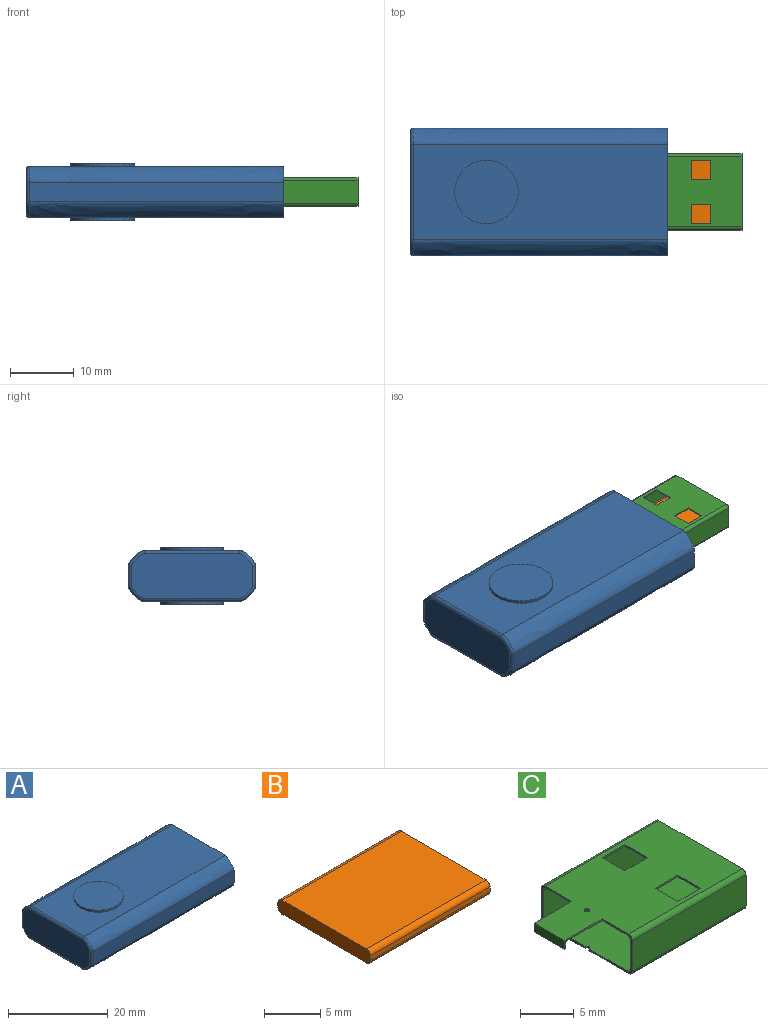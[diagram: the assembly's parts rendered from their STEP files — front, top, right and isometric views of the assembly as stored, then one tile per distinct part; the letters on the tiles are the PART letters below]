
ASSEMBLY  parts=3 mates=2
PART A: 31 faces, bbox 44.5x20.5x9.5 mm
  f0: plane 40x3mm, normal (0,1,0), area 120mm2, adj f12,f14,f16,f21
  f1: plane 40x15mm, normal (0,0,1), area 521.5mm2, adj f12,f15,f16,f25,f27
  f2: plane 40x3mm, normal (0,-1,0), area 120mm2, adj f12,f13,f15,f24
  f3: plane 40x11mm, normal (0,0,-1), area 440mm2, adj f4,f10,f12,f17
  f4: cylinder r=0.5mm len=40mm, axis (1,0,0), area 31.4mm2, adj f3,f5,f12,f17
  f5: plane 40x3.5mm, normal (0,-1,0), area 140mm2, adj f4,f6,f12,f17
  f6: cylinder r=0.5mm len=40mm, axis (1,0,0), area 31.4mm2, adj f5,f7,f12,f17
  f7: plane 40x11mm, normal (0,0,1), area 440mm2, adj f6,f8,f12,f17
  f8: cylinder r=0.5mm len=40mm, axis (1,0,0), area 31.4mm2, adj f7,f9,f12,f17
  f9: plane 40x3.5mm, normal (0,1,0), area 140mm2, adj f8,f10,f12,f17
  f10: cylinder r=0.5mm len=40mm, axis (1,0,0), area 31.4mm2, adj f3,f9,f12,f17
  f11: plane 40x15mm, normal (0,0,-1), area 521.5mm2, adj f12,f13,f14,f20,f29
  f12: plane 20.5x8.5mm, normal (1,0,0), area 98.3mm2, adj f0,f1,f2,f3,f4,f5,f6,f7
  f13: bspline ~44x2.5mm, area 149mm2, adj f2,f11,f12,f22
  f14: bspline ~44x2.5mm, area 149mm2, adj f0,f11,f12,f19
  f15: bspline ~44x2.5mm, area 149mm2, adj f1,f2,f12,f26
  f16: bspline ~44x2.5mm, area 149mm2, adj f0,f1,f12,f23
  f17: plane 12x4.5mm, normal (1,0,0), area 53.8mm2, adj f3,f4,f5,f6,f7,f8,f9,f10
  f18: plane 19x7mm, normal (-1,0,0), area 127.5mm2, adj f19,f20,f21,f22,f23,f24,f25,f26
  f19: bspline ~3.12x2.74mm, area 2.7mm2, adj f14,f18,f20,f21
  f20: cylinder r=0.5mm len=15mm, axis (0,1,0), area 11.8mm2, adj f11,f18,f19,f22
  f21: cylinder r=0.5mm len=3mm, axis (0,0,1), area 2.4mm2, adj f0,f18,f19,f23
  f22: bspline ~3.12x2.74mm, area 2.7mm2, adj f13,f18,f20,f24
  f23: bspline ~3.12x2.74mm, area 2.7mm2, adj f16,f18,f21,f25
  f24: cylinder r=0.5mm len=3mm, axis (0,0,-1), area 2.4mm2, adj f2,f18,f22,f26
  f25: cylinder r=0.5mm len=15mm, axis (0,-1,0), area 11.8mm2, adj f1,f18,f23,f26
  f26: bspline ~3.12x2.74mm, area 2.7mm2, adj f15,f18,f24,f25
  f27: cylinder r=5mm len=10mm, axis (0,0,-1), area 15.7mm2, adj f1,f28
  f28: plane 10x10mm, normal (0,0,1), area 78.5mm2, adj f27
  f29: cylinder r=5mm len=10mm, axis (0,0,1), area 15.7mm2, adj f11,f30
  f30: plane 10x10mm, normal (0,0,-1), area 78.5mm2, adj f29
PART B: 10 faces, bbox 15x11.6x1.5 mm
  f0: plane 11.6x1.5mm, normal (-1,0,0), area 17.2mm2, adj f1,f2,f3,f4,f5,f6,f7,f8
  f1: plane 15x0.5mm, normal (0,-1,0), area 7.5mm2, adj f0,f2,f8,f9
  f2: cylinder r=0.5mm len=15mm, axis (1,0,0), area 11.8mm2, adj f0,f1,f3,f9
  f3: plane 15x10.6mm, normal (0,0,-1), area 159mm2, adj f0,f2,f4,f9
  f4: cylinder r=0.5mm len=15mm, axis (1,0,0), area 11.8mm2, adj f0,f3,f5,f9
  f5: plane 15x0.5mm, normal (0,1,0), area 7.5mm2, adj f0,f4,f6,f9
  f6: cylinder r=0.5mm len=15mm, axis (1,0,0), area 11.8mm2, adj f0,f5,f7,f9
  f7: plane 15x10.6mm, normal (0,0,1), area 159mm2, adj f0,f6,f8,f9
  f8: cylinder r=0.5mm len=15mm, axis (1,0,0), area 11.8mm2, adj f0,f1,f7,f9
  f9: plane 11.6x1.5mm, normal (1,0,0), area 17.2mm2, adj f1,f2,f3,f4,f5,f6,f7,f8
PART C: 42 faces, bbox 20x12x4.5 mm
  f0: cylinder r=0.25mm len=0.5mm, axis (0,0,-1), area 0.2mm2, adj f10,f11,f24,f31
  f1: plane 12x4.5mm, normal (1,0,0), area 6.4mm2, adj f13,f14,f23,f24,f29,f30,f31,f32
  f2: plane 3x0.2mm, normal (0,1,0), area 0.6mm2, adj f3,f8,f24,f31
  f3: plane 3x0.2mm, normal (1,0,0), area 0.6mm2, adj f2,f4,f24,f31
  f4: plane 3x0.2mm, normal (0,-1,0), area 0.6mm2, adj f3,f8,f24,f31
  f5: plane 3x0.2mm, normal (1,0,0), area 0.6mm2, adj f6,f9,f24,f31
  f6: plane 3x0.2mm, normal (0,-1,0), area 0.6mm2, adj f5,f7,f24,f31
  f7: plane 3x0.2mm, normal (-1,0,0), area 0.6mm2, adj f6,f9,f24,f31
  f8: plane 3x0.2mm, normal (-1,0,0), area 0.6mm2, adj f2,f4,f24,f31
  f9: plane 3x0.2mm, normal (0,1,0), area 0.6mm2, adj f5,f7,f24,f31
  f10: plane 5.75x4.5mm, normal (-1,0,0), area 2.8mm2, adj f0,f13,f23,f24,f27,f30,f31,f32
  f11: plane 5.75x4.5mm, normal (-1,0,0), area 2.8mm2, adj f0,f14,f23,f24,f25,f29,f31,f32
  f12: cylinder r=0.25mm len=0.5mm, axis (0,0,-1), area 0.3mm2, adj f23,f32
  f13: plane 15x3.5mm, normal (0,-1,0), area 52.5mm2, adj f1,f10,f39,f41
  f14: plane 15x3.5mm, normal (0,1,0), area 52.5mm2, adj f1,f11,f38,f40
  f15: plane 3x0.2mm, normal (0,1,0), area 0.6mm2, adj f16,f21,f23,f32
  f16: plane 3x0.2mm, normal (1,0,0), area 0.6mm2, adj f15,f17,f23,f32
  f17: plane 3x0.2mm, normal (0,-1,0), area 0.6mm2, adj f16,f21,f23,f32
  f18: plane 3x0.2mm, normal (1,0,0), area 0.6mm2, adj f19,f22,f23,f32
  f19: plane 3x0.2mm, normal (0,-1,0), area 0.6mm2, adj f18,f20,f23,f32
  f20: plane 3x0.2mm, normal (-1,0,0), area 0.6mm2, adj f19,f22,f23,f32
  f21: plane 3x0.2mm, normal (-1,0,0), area 0.6mm2, adj f15,f17,f23,f32
  f22: plane 3x0.2mm, normal (0,1,0), area 0.6mm2, adj f18,f20,f23,f32
  f23: plane 20x11mm, normal (0,0,1), area 166.8mm2, adj f1,f10,f11,f12,f15,f16,f17,f18
  f24: plane 15x11mm, normal (0,0,-1), area 146.9mm2, adj f0,f1,f2,f3,f4,f5,f6,f7
  f25: plane 5x1mm, normal (0,1,0), area 1.2mm2, adj f11,f23,f26,f28,f32,f33
  f26: plane 4x1mm, normal (-1,0,0), area 4mm2, adj f23,f25,f27,f28
  f27: plane 5x1mm, normal (0,-1,0), area 1.2mm2, adj f10,f23,f26,f28,f32,f33
  f28: plane 4x0.2mm, normal (0,0,-1), area 0.8mm2, adj f25,f26,f27,f33
  f29: plane 15x3.1mm, normal (0,-1,0), area 46.5mm2, adj f1,f11,f34,f36
  f30: plane 15x3.1mm, normal (0,1,0), area 46.5mm2, adj f1,f10,f35,f37
  f31: plane 15x10.6mm, normal (0,0,1), area 140.9mm2, adj f0,f1,f2,f3,f4,f5,f6,f7
  f32: plane 19.8x10.6mm, normal (0,0,-1), area 160mm2, adj f1,f10,f11,f12,f15,f16,f17,f18
  f33: plane 4x0.8mm, normal (1,0,0), area 3.2mm2, adj f25,f27,f28,f32
  f34: cylinder r=0.5mm len=15mm, axis (1,0,0), area 11.8mm2, adj f1,f11,f29,f32
  f35: cylinder r=0.5mm len=15mm, axis (-1,0,0), area 11.8mm2, adj f1,f10,f30,f32
  f36: cylinder r=0.5mm len=15mm, axis (-1,0,0), area 11.8mm2, adj f1,f11,f29,f31
  f37: cylinder r=0.5mm len=15mm, axis (1,0,0), area 11.8mm2, adj f1,f10,f30,f31
  f38: cylinder r=0.5mm len=15mm, axis (-1,0,0), area 11.8mm2, adj f1,f11,f14,f24
  f39: cylinder r=0.5mm len=15mm, axis (1,0,0), area 11.8mm2, adj f1,f10,f13,f24
  f40: cylinder r=0.5mm len=15mm, axis (1,0,0), area 11.8mm2, adj f1,f11,f14,f23
  f41: cylinder r=0.5mm len=15mm, axis (-1,0,0), area 11.8mm2, adj f1,f10,f13,f23
PLACE A t=(-10.21,-20.18,11.52)mm
PLACE B t=(-10.68,-20.18,11.42)mm
PLACE C t=(-10.56,-20.18,11.52)mm
MATE slider C.f1 <-> A.f12  axis (1,0,0) through (4.44,-20.18,13.77)mm
MATE fastened B.f3 <-> C.f31  axis (0,0,-1) through (-3.18,-20.18,9.47)mm
